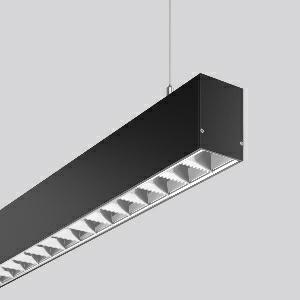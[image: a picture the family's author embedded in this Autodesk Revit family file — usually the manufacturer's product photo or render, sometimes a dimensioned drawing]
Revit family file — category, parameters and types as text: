
# Revit family: less_is_more_50_312339_003_1_6ee4
name_source: partatom
category: Lighting Fixtures
units: mm (PartAtom-declared; Revit-internal decimal feet)

## family parameters
Cut with Voids When Loaded = No
Host = Face
Light Source = No
Part Type = Normal
Room Calculation Point = No
Round Connector Dimension = Use Diameter
Shared = No

## types (1)
- LESS IS MORE 50 (1 x LED Modul 840, 6200 lm, 4000)
    Apparent Load = 48 VA
    CIE Flux Codes = 95 100 100 100 100
    Color Rendering = 80
    Color Temperature = 4000
    Default Elevation = 1800 mm
    Description = Series: LESS IS MORE 50
Linear pendant luminaire for aesthetically sophisticated lighting. Housing: extruded aluminium profile, powder-coated. End cap aluminium powder-coated. Canopy made of aluminium, powder-coated. Alea optical system: Reflector structure (ABS, Aluminium-coated, highly polished) with integrated diffuser made of non-yellowing plastic (PMMA) opal for glare-free light at the workstation (screen-compliant according to EN 12464-1). Direct light emission. Suitable for pendant. 2-point steel cable suspension freely positionable and infinitely height-adjustable. Special lengths available on request. LED unit with integrated converter interchangeable and removable. Suitable for through-wiring. With sensors or as a safety luminaire on request. 
Colour: deep black, matt (RAL 9005)
Length: 1967 mm
Width: 57 mm
Height: 75 mm
Suspension length: 2000 mm
Lamp: LED
Socket: without socket
Colour temperature: 4000K
Colour rendering index (CRI): 80
System power: 48 W
Rated luminous flux: 6200 lm
Luminous efficiency: 129 lm/W
Control gear: Regulated power supply
Protection class: I
Type of protection: IP 20
    Height = 75 mm
    Lamp = 1 x LED Modul 840
    Lamp Light Flux = 6200 lm
    Lamp count = 1
    Length = 1967 mm
    Lifetime = 50000 h
    Luminous efficacy = 129 lm/W
    Manufacturer = RZB
    ModVariant = No
    Model = 312339.003.1
    Mounting Place = Ceiling
    Mounting Type = Pendant
    Number of Poles = 1
    OnlyDefault = Yes
    Power Factor = 1
    Product Name = LESS IS MORE 50
    Product group = Pendant LED linear luminaires
    ProductGroupID = 907
    Protection Class = Protection class I
    Protection Degree = IP 20
    RLX_Detail_Level = 1
    RLX_Emergency_Light_Flux = 0 lm
    RLX_Emergency_Type = 0
    RLX_Emergency_Type_DB = No
    RlxData = <blob elided: 39573 chars, md5=0b62c658>
    Socket = socket
    Standby Power = 0 W
    System Light Flux = 6200 lm
    System Power = 48 W
    Type Comments = Product without accessories
    Type Image = 312342.003.jpg
    URL = http://relux.com
    VarID = ---
    Voltage = 230 V
    Voltage Range = 220-240 V
    Weight = 0.00 kg
    Width = 57 mm

## geometry (parser evidence)
native form markers: Blend x4, Sweep x10
no freeform markers — native parametric forms only
